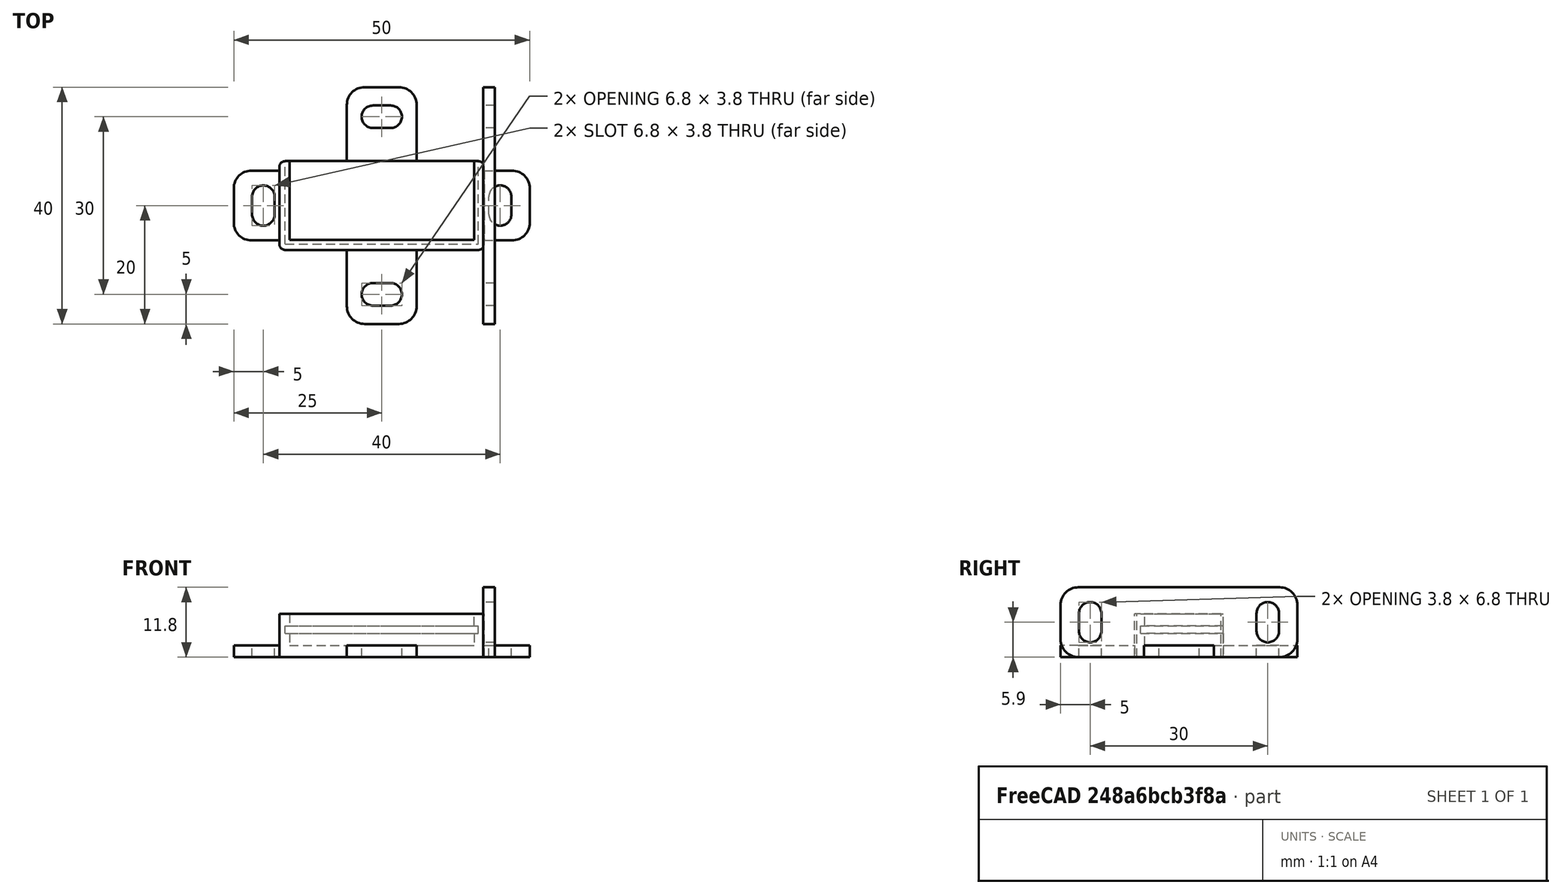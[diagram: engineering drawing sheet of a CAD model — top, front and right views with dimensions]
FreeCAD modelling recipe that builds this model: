
FCSTD DOCUMENT  (FreeCAD 0.19R23578 (Git))
Label: kxdjs2002.1
License: FreeArt
LicenseURL: http://artlibre.org/licence/lal
objects: Part::Box×9, Part::MultiFuse×6, Part::Fillet×3, Part::Feature×3, Part::Cut×3, App::Part×3, Spreadsheet::Sheet×1
note: 24 computed .brp shape members not serialized (recipe doc carries the construction recipe); baked Part::Feature solids carry a one-line shape summary decoded from their .brp

FEATURE [Spreadsheet::Sheet] Spreadsheet  label="p"
  cells = A1=pcb_x; B1(pcb_x)=32.6; A2=pcb_y; B2(pcb_y)=14; A3=pcb_z; B3(pcb_z)=1.3; A4=pcb_under; B4(pcb_under)=2; A5=side_wall; B5(side_wall)=1; A6=pcb_side_lane; B6(pcb_side_lane)=0.7; A7=bottom_wall; B7(bottom_wall)=2; A8=pcb_above; B8(pcb_above)=2; A9=box_x; B9(box_x)==pcb_x + 2 * side_wall; A10=box_y; B10(box_y)==pcb_y + side_wall; A11=box_z; B11(box_z)==bottom_wall + pcb_under + pcb_z + pcb_above
FEATURE [Part::Box] Box  label="external cube"
  AttacherType = Attacher::AttachEngine3D
  Height = 7.3
  Length = 34.6
  Width = 15
  expr: Length = <<p>>.box_x
  expr: Width = <<p>>.box_y
  expr: Height = <<p>>.box_z
FEATURE [Part::Box] Box006  label="internal cube"
  AttacherType = Attacher::AttachEngine3D
  Height = 5.3
  Length = 31.2
  Placement = pos=(1.7,1.7,2) rot=(0,0,1;0rad)
  Width = 13.6
  expr: Length = <<p>>.pcb_x - 2 * <<p>>.pcb_side_lane
  expr: Width = <<p>>.pcb_y - 2 * <<p>>.pcb_side_lane + <<p>>.side_wall
  expr: Height = <<p>>.pcb_under + <<p>>.pcb_z + <<p>>.pcb_above
  expr: .Placement.Base.z = <<p>>.bottom_wall
  expr: .Placement.Base.x = <<p>>.side_wall + <<p>>.pcb_side_lane
  expr: .Placement.Base.y = <<p>>.side_wall + <<p>>.pcb_side_lane
FEATURE [Part::Box] Box007  label="pcb extract cube"
  AttacherType = Attacher::AttachEngine3D
  Height = 1.3
  Length = 32.6
  Placement = pos=(1,1,4) rot=(0,0,1;0rad)
  Width = 14
  expr: Height = <<p>>.pcb_z
  expr: .Placement.Base.z = <<p>>.bottom_wall + <<p>>.pcb_under
  expr: Width = <<p>>.pcb_y
  expr: Length = <<p>>.pcb_x
  expr: .Placement.Base.x = <<p>>.side_wall
  expr: .Placement.Base.y = <<p>>.side_wall
FEATURE [Part::MultiFuse] Fusion  label="extract fusion"
  Shapes = -> [Box006,Box007]
FEATURE [Part::Fillet] Fillet  label="external fillet"
  Base = -> Box
  Edges = 4 edges r=1: [Edge1,Edge3,Edge5,Edge7]
FEATURE [Part::Box] Box008  label="external cube001"
  AttacherType = Attacher::AttachEngine3D
  Height = 7.3
  Length = 34.6
  Width = 15
  expr: Length = <<p>>.box_x
  expr: Width = <<p>>.box_y
  expr: Height = <<p>>.box_z
FEATURE [Part::Fillet] Fillet001  label="external fillet001"
  Base = -> Box008
  Edges = 4 edges r=1: [Edge1,Edge3,Edge5,Edge7]
FEATURE [Part::Box] Box009  label="internal cube001"
  AttacherType = Attacher::AttachEngine3D
  Height = 5.3
  Length = 31.2
  Placement = pos=(1.7,1.7,2) rot=(0,0,1;0rad)
  Width = 13.6
  expr: Length = <<p>>.pcb_x - 2 * <<p>>.pcb_side_lane
  expr: Width = <<p>>.pcb_y - 2 * <<p>>.pcb_side_lane + <<p>>.side_wall
  expr: Height = <<p>>.pcb_under + <<p>>.pcb_z + <<p>>.pcb_above
  expr: .Placement.Base.z = <<p>>.bottom_wall
  expr: .Placement.Base.x = <<p>>.side_wall + <<p>>.pcb_side_lane
  expr: .Placement.Base.y = <<p>>.side_wall + <<p>>.pcb_side_lane
FEATURE [Part::Box] Box010  label="pcb extract cube001"
  AttacherType = Attacher::AttachEngine3D
  Height = 1.3
  Length = 32.6
  Placement = pos=(1,1,4) rot=(0,0,1;0rad)
  Width = 14
  expr: Height = <<p>>.pcb_z
  expr: .Placement.Base.z = <<p>>.bottom_wall + <<p>>.pcb_under
  expr: Width = <<p>>.pcb_y
  expr: Length = <<p>>.pcb_x
  expr: .Placement.Base.x = <<p>>.side_wall
  expr: .Placement.Base.y = <<p>>.side_wall
FEATURE [Part::MultiFuse] Fusion003  label="extract fusion001"
  Shapes = -> [Box009,Box010]
FEATURE [Part::Box] Box011  label="external cube002"
  AttacherType = Attacher::AttachEngine3D
  Height = 7.3
  Length = 34.6
  Width = 15
  expr: Height = <<p>>.box_z
  expr: Width = <<p>>.box_y
  expr: Length = <<p>>.box_x
FEATURE [Part::Fillet] Fillet002  label="external fillet002"
  Base = -> Box011
  Edges = 4 edges r=1: [Edge1,Edge3,Edge5,Edge7]
FEATURE [Part::Box] Box012  label="internal cube002"
  AttacherType = Attacher::AttachEngine3D
  Height = 5.3
  Length = 31.2
  Placement = pos=(1.7,1.7,2) rot=(0,0,1;0rad)
  Width = 13.6
  expr: .Placement.Base.y = <<p>>.side_wall + <<p>>.pcb_side_lane
  expr: .Placement.Base.x = <<p>>.side_wall + <<p>>.pcb_side_lane
  expr: .Placement.Base.z = <<p>>.bottom_wall
  expr: Height = <<p>>.pcb_under + <<p>>.pcb_z + <<p>>.pcb_above
  expr: Width = <<p>>.pcb_y - 2 * <<p>>.pcb_side_lane + <<p>>.side_wall
  expr: Length = <<p>>.pcb_x - 2 * <<p>>.pcb_side_lane
FEATURE [Part::Box] Box013  label="pcb extract cube002"
  AttacherType = Attacher::AttachEngine3D
  Height = 1.3
  Length = 32.6
  Placement = pos=(1,1,4) rot=(0,0,1;0rad)
  Width = 14
  expr: .Placement.Base.y = <<p>>.side_wall
  expr: .Placement.Base.x = <<p>>.side_wall
  expr: Length = <<p>>.pcb_x
  expr: Width = <<p>>.pcb_y
  expr: .Placement.Base.z = <<p>>.bottom_wall + <<p>>.pcb_under
  expr: Height = <<p>>.pcb_z
FEATURE [Part::MultiFuse] Fusion005  label="extract fusion002"
  Shapes = -> [Box012,Box013]
FEATURE [Part::Feature] Cut003001  label="attach plane x dir001"
  Placement = pos=(-7.7,1.6,0) rot=(0,0,1;0rad)
  shape: bbox 50 x 11.8 x 2 mm, 18 faces (baked)
FEATURE [Part::MultiFuse] Fusion001  label="outer fusion"
  Shapes = -> [Fillet,Cut003001]
FEATURE [Part::Cut] Cut  label="body cut"
  Base = -> Fusion001
  Tool = -> Fusion
FEATURE [App::Part] Part  label="kxdjs2002.1 pcb box part"
  Group = -> [Box006,Box007,Fusion,Cut]
  Origin = -> Origin
FEATURE [Part::Feature] Cut003007  label="attach plane y dir001"
  Placement = pos=(36.4,-12.5,0) rot=(0,1,0;4.71239rad)
  shape: bbox 2 x 40 x 11.8 mm, 20 faces (baked)
FEATURE [Part::MultiFuse] Fusion004  label="outer fusion002"
  Shapes = -> [Fillet002,Cut003007]
FEATURE [Part::Cut] Cut003004  label="body cut z"
  Base = -> Fusion004
  Tool = -> Fusion005
FEATURE [App::Part] Part002  label="kxdjs2002.1 pcb box z part"
  Group = -> [Fusion005,Box013,Fillet002,Box011,Fusion004,Box012,Cut003004]
  Origin = -> Origin002
FEATURE [Part::Feature] Cut003008  label="attach plane y dir"
  Placement = pos=(11.4,-12.5,0) rot=(0,0,1;0rad)
  shape: bbox 11.8 x 40 x 2 mm, 20 faces (baked)
FEATURE [Part::MultiFuse] Fusion002  label="outer fusion001"
  Shapes = -> [Fillet001,Cut003008]
FEATURE [Part::Cut] Cut003003  label="body cut y"
  Base = -> Fusion002
  Tool = -> Fusion003
FEATURE [App::Part] Part001  label="kxdjs2002.1 pcb box y part"
  Group = -> [Fusion003,Box010,Fillet001,Box008,Fusion002,Box009,Cut003003]
  Origin = -> Origin001
